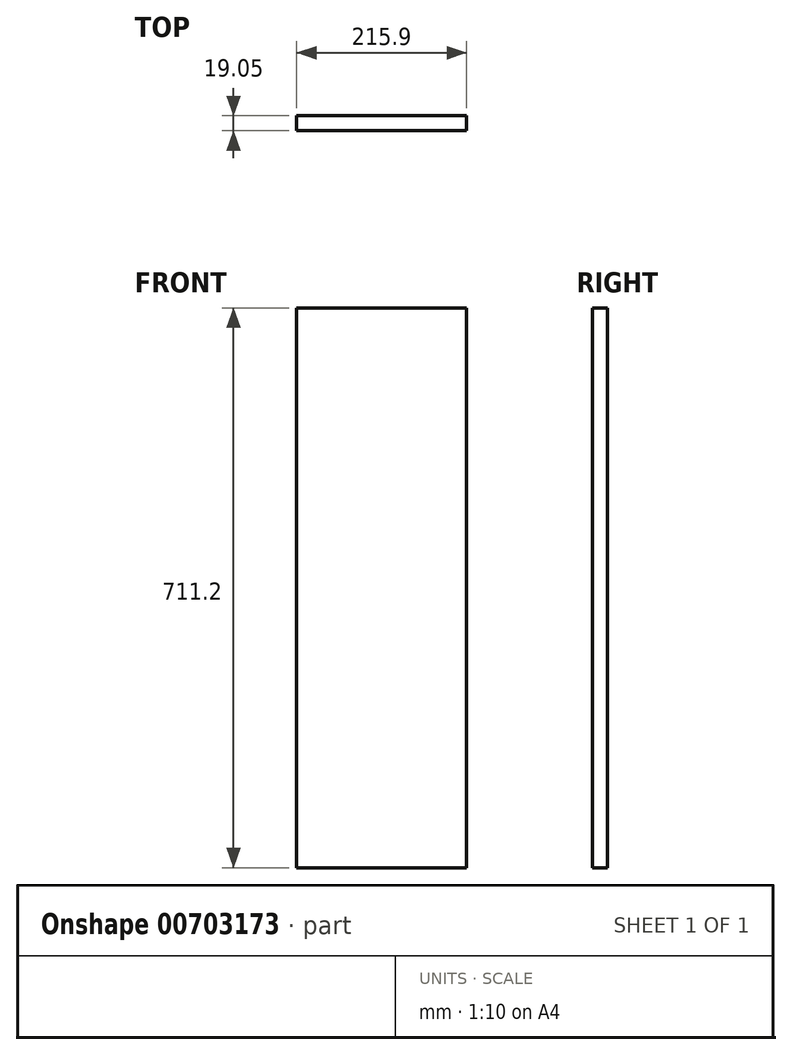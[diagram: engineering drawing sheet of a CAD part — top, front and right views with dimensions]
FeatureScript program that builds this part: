
annotation { "Feature Type Name" : "Feature", "Feature Type Description" : "" }
export const myFeature = defineFeature(function(context is Context, id is Id, definition is map)
    precondition{}
    {
        {
            var Q0;
            Q0=qCreatedBy(makeId("Front.planeOp"),FACE);
            var sketch = newSketch(context, id + "F0", { "sketchPlane" : qUnion([Q0])});
            skLineSegment(sketch, "E0.bottom", {"start": v(107.95, 355.6) * mm, "end": v(-107.95, 355.6) * mm});
            skLineSegment(sketch, "E0.top", {"start": v(107.95, -355.6) * mm, "end": v(-107.95, -355.6) * mm});
            skLineSegment(sketch, "E0.left", {"start": v(107.95, 355.6) * mm, "end": v(107.95, -355.6) * mm});
            skLineSegment(sketch, "E0.right", {"start": v(-107.95, 355.6) * mm, "end": v(-107.95, -355.6) * mm});
            skPoint(sketch, "E0.middle", {"position": v(0, 0) * mm});
            skSolve(sketch);
        }
        {
            var Q0;
            Q0=makeQuery(id+"F0.imprint","IMPRINT",FACE,{"disambiguationData":[TD([[makeQuery(id+"F0.imprint","IMPRINT",EDGE,{"derivedFrom":sQuery(id+"F0.wireOp",EDGE,"E0.bottom")}),1.0]])]});
            extrude(context, id + "F1", {"entities" : qUnion([Q0]), "depth" : 19.05 * mm, "offsetDistance" : 25.4 * mm});
        }
    });
